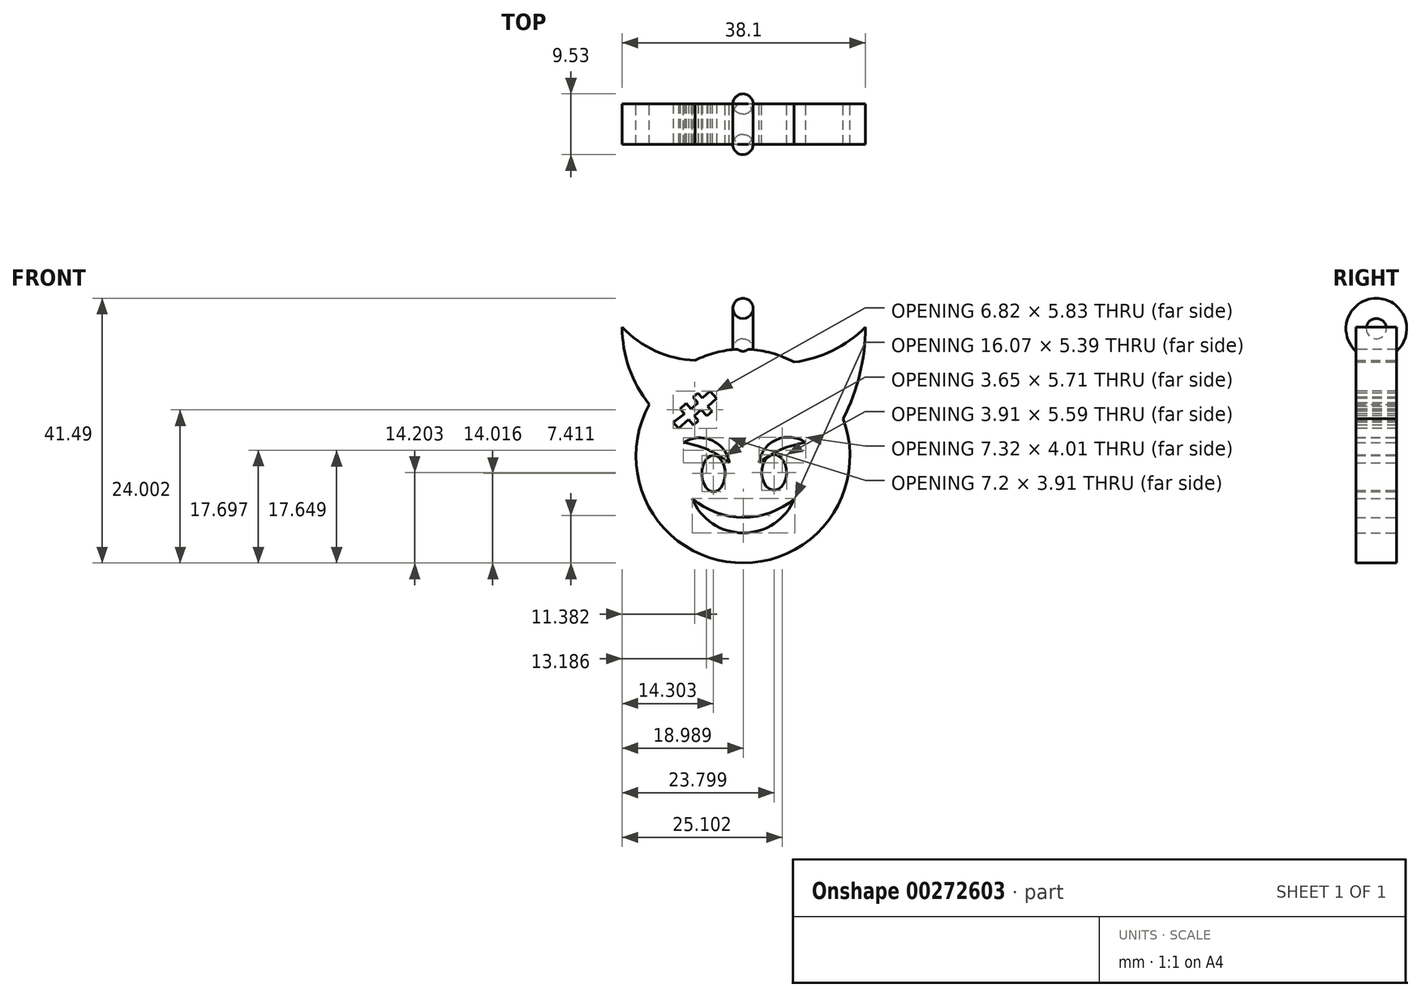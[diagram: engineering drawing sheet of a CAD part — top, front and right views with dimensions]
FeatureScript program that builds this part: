
annotation { "Feature Type Name" : "Feature", "Feature Type Description" : "" }
export const myFeature = defineFeature(function(context is Context, id is Id, definition is map)
    precondition{}
    {
        {
            var Q0;
            Q0=qCreatedBy(makeId("Front.planeOp"),FACE);
            var sketch = newSketch(context, id + "F0", { "sketchPlane" : qUnion([Q0])});
            skArc(sketch, "E0", {"start": v(8.01, 14.72) * mm, "mid": v(0.29, 16.76) * mm, "end": v(-7.5, 14.99) * mm});
            skArc(sketch, "E1", {"start": v(-18.92, 20.2) * mm, "mid": v(-17.83, 13.8) * mm, "end": v(-14.67, 8.1) * mm});
            skArc(sketch, "E2", {"start": v(-18.92, 20.2) * mm, "mid": v(-13.72, 16.49) * mm, "end": v(-7.5, 14.99) * mm});
            skArc(sketch, "E3", {"start": v(8.01, 14.72) * mm, "mid": v(14.05, 16.53) * mm, "end": v(19.18, 20.2) * mm});
            skArc(sketch, "E4", {"start": v(15.7, 5.86) * mm, "mid": v(18.3, 12.82) * mm, "end": v(19.18, 20.2) * mm});
            skEllipse(sketch, "E5", {"center": v(-4.62, -2.74) * mm, "majorRadius": 2.85 * mm, "minorRadius": 1.83 * mm, "majorAxis": v(0, 1)});
            skEllipse(sketch, "E6", {"center": v(4.88, -2.56) * mm, "majorRadius": 2.8 * mm, "minorRadius": 1.96 * mm, "majorAxis": v(0, 1)});
            skArc(sketch, "E7", {"start": v(-2.13, -1.07) * mm, "mid": v(-5.52, 1) * mm, "end": v(-9.33, 2.1) * mm});
            skArc(sketch, "E8", {"start": v(-2.13, -1.07) * mm, "mid": v(-4.88, 2.47) * mm, "end": v(-9.33, 2.1) * mm});
            skArc(sketch, "E9", {"start": v(9.84, 2.1) * mm, "mid": v(5.96, 1.02) * mm, "end": v(2.52, -1.07) * mm});
            skArc(sketch, "E10", {"start": v(9.84, 2.1) * mm, "mid": v(5.29, 2.59) * mm, "end": v(2.52, -1.07) * mm});
            skArc(sketch, "E11", {"start": v(-7.97, -6.65) * mm, "mid": v(0.07, -12.04) * mm, "end": v(8.1, -6.65) * mm});
            skArc(sketch, "E12", {"start": v(-7.97, -6.65) * mm, "mid": v(0.07, -9.62) * mm, "end": v(8.1, -6.65) * mm});
            skArc(sketch, "E13.trimOffspring", {"start": v(-14.67, 8.1) * mm, "mid": v(-1.23, -16.72) * mm, "end": v(15.7, 5.86) * mm});
            skSolve(sketch);
        }
        {
            var Q0;
            Q0=makeQuery(id+"F0.imprint","IMPRINT",FACE,{"disambiguationData":[TD([[makeQuery(id+"F0.imprint","IMPRINT",EDGE,{"derivedFrom":sQuery(id+"F0.wireOp",EDGE,"E1")}),1.0]])]});
            extrude(context, id + "F1", {"entities" : qUnion([Q0]), "depth" : 6.35 * mm});
        }
        {
            var Q0;
            Q0=makeQuery(id+"F1.opExtrude","CAP_FACE",FACE,{"disambiguationData":[OSD([sQuery(id+"F0.wireOp",EDGE,"E0"),sQuery(id+"F0.wireOp",EDGE,"E1"),sQuery(id+"F0.wireOp",EDGE,"E2"),sQuery(id+"F0.wireOp",EDGE,"E3"),sQuery(id+"F0.wireOp",EDGE,"E4"),sQuery(id+"F0.wireOp",EDGE,"E5"),sQuery(id+"F0.wireOp",EDGE,"E6"),sQuery(id+"F0.wireOp",EDGE,"E7"),sQuery(id+"F0.wireOp",EDGE,"E8"),sQuery(id+"F0.wireOp",EDGE,"E9"),sQuery(id+"F0.wireOp",EDGE,"E10"),sQuery(id+"F0.wireOp",EDGE,"E11"),sQuery(id+"F0.wireOp",EDGE,"E12"),sQuery(id+"F0.wireOp",EDGE,"E13.trimOffspring")])],"isStart":false});
            var sketch = newSketch(context, id + "F2", { "sketchPlane" : qUnion([Q0])});
            skLineSegment(sketch, "E14", {"start": v(-10.95, 5.31) * mm, "end": v(-10.1, 4.33) * mm});
            skLineSegment(sketch, "E15", {"start": v(-10.1, 4.33) * mm, "end": v(-8.5, 5.72) * mm});
            skLineSegment(sketch, "E16", {"start": v(-8.5, 5.72) * mm, "end": v(-7.75, 4.85) * mm});
            skLineSegment(sketch, "E17", {"start": v(-7.75, 4.85) * mm, "end": v(-6.98, 5.51) * mm});
            skLineSegment(sketch, "E18", {"start": v(-6.98, 5.51) * mm, "end": v(-7.65, 6.28) * mm});
            skLineSegment(sketch, "E19", {"start": v(-7.65, 6.28) * mm, "end": v(-6.53, 7.26) * mm});
            skLineSegment(sketch, "E20", {"start": v(-6.53, 7.26) * mm, "end": v(-5.68, 6.28) * mm});
            skLineSegment(sketch, "E21", {"start": v(-5.68, 6.28) * mm, "end": v(-4.85, 7) * mm});
            skLineSegment(sketch, "E22", {"start": v(-4.85, 7) * mm, "end": v(-5.53, 7.8) * mm});
            skLineSegment(sketch, "E23", {"start": v(-5.53, 7.8) * mm, "end": v(-4.13, 9) * mm});
            skLineSegment(sketch, "E24", {"start": v(-4.13, 9) * mm, "end": v(-5.12, 10.15) * mm});
            skLineSegment(sketch, "E25", {"start": v(-5.12, 10.15) * mm, "end": v(-6.37, 9.07) * mm});
            skLineSegment(sketch, "E26", {"start": v(-6.37, 9.07) * mm, "end": v(-7.05, 9.86) * mm});
            skLineSegment(sketch, "E27", {"start": v(-7.05, 9.86) * mm, "end": v(-7.8, 9.2) * mm});
            skLineSegment(sketch, "E28", {"start": v(-7.8, 9.2) * mm, "end": v(-7.05, 8.34) * mm});
            skLineSegment(sketch, "E29", {"start": v(-7.05, 8.34) * mm, "end": v(-8.11, 7.41) * mm});
            skLineSegment(sketch, "E30", {"start": v(-8.11, 7.41) * mm, "end": v(-8.87, 8.28) * mm});
            skLineSegment(sketch, "E31", {"start": v(-8.87, 8.28) * mm, "end": v(-9.87, 7.41) * mm});
            skLineSegment(sketch, "E32", {"start": v(-9.87, 7.41) * mm, "end": v(-9.17, 6.6) * mm});
            skLineSegment(sketch, "E33", {"start": v(-9.17, 6.6) * mm, "end": v(-10.95, 5.31) * mm});
            skSolve(sketch);
        }
        {
            var Q0;
            Q0=makeQuery(id+"F2.imprint","IMPRINT",FACE,{"disambiguationData":[TD([[makeQuery(id+"F2.imprint","IMPRINT",EDGE,{"derivedFrom":sQuery(id+"F2.wireOp",EDGE,"E14")}),1.0]])]});
            extrude(context, id + "F3", {"entities" : qUnion([Q0]), "operationType" : NewBodyOperationType.REMOVE, "oppositeDirection" : true, "depth" : 6.35 * mm});
        }
        {
            var Q0;
            Q0=qCreatedBy(makeId("Front.planeOp"),FACE);
            cPlane(context, id + "F4", {"entities" : qUnion([Q0]), "cplaneType" : CPlaneType.OFFSET, "offset" : 3.17 * mm, "width" : 152.4 * mm, "height" : 152.4 * mm});
        }
        {
            var Q0;
            Q0=qCreatedBy(id+"F4.planeOp",FACE);
            var sketch = newSketch(context, id + "F5", { "sketchPlane" : qUnion([Q0])});
            skCircle(sketch, "E34", {"center": v(0, 16.8) * mm, "radius": 1.59 * mm});
            skLineSegment(sketch, "E35", {"start": v(0, 16.8) * mm, "end": v(0, 19.97) * mm});
            skLineSegment(sketch, "E36", {"start": v(0, 19.97) * mm, "end": v(-14.89, 19.97) * mm});
            skSolve(sketch);
        }
        {
            var Q0;
            Q0 = qSketchRegion(id + "F5", true);
            var Q1;
            Q1=sQuery(id+"F5.wireOp",EDGE,"E36");
            revolve(context, id + "F6", {"operationType" : NewBodyOperationType.ADD, "entities" : qUnion([Q0]), "axis" : qUnion([Q1]), "revolveType" : RevolveType.FULL});
        }
    });
